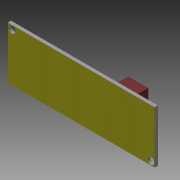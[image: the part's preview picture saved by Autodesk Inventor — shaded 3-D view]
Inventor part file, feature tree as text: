
AUTODESK INVENTOR PART (.ipt)
format: ipt  version: 2015 (Build 190159000, 159)  size: 141,824 bytes
history: native  units: mm
features: extrude x3, sketch x2
ambient origin geometry x8: Origin, YZ Plane, XZ Plane, XY Plane, X Axis, Y Axis, Z Axis, Center Point
bodies: Solid1 (feature_tree)
feature tree (5):
  sketch  "Sketch1"  dims[d0=73.55mm d1=26.14mm]
  extrude  "Extrusion1"  Depth=26.14mm
  extrude  "Extrusion2"  Depth=2.0mm
  extrude  "Extrusion3"  Depth=2.0mm
  sketch  "Sketch2"  dims[d2=3.5mm d3=2.0mm d4=2.0mm d5=3.5mm d6=2.0mm d7=2.0mm d8=10.0mm d9=11.68mm d10=12.0mm d11=2.0mm d12=6.26mm d13=6.26mm d14=6.26mm d15=6.26mm d16=10.0mm d17=6.26mm d18=6.26mm d19=10.0mm d20=6.26mm d21=6.26mm d22=10.0mm d23=6.984546mm d24=1.6mm d25=0.0mm d26=8.76mm d27=0.0mm d28=6.0mm d29=0.0mm]
